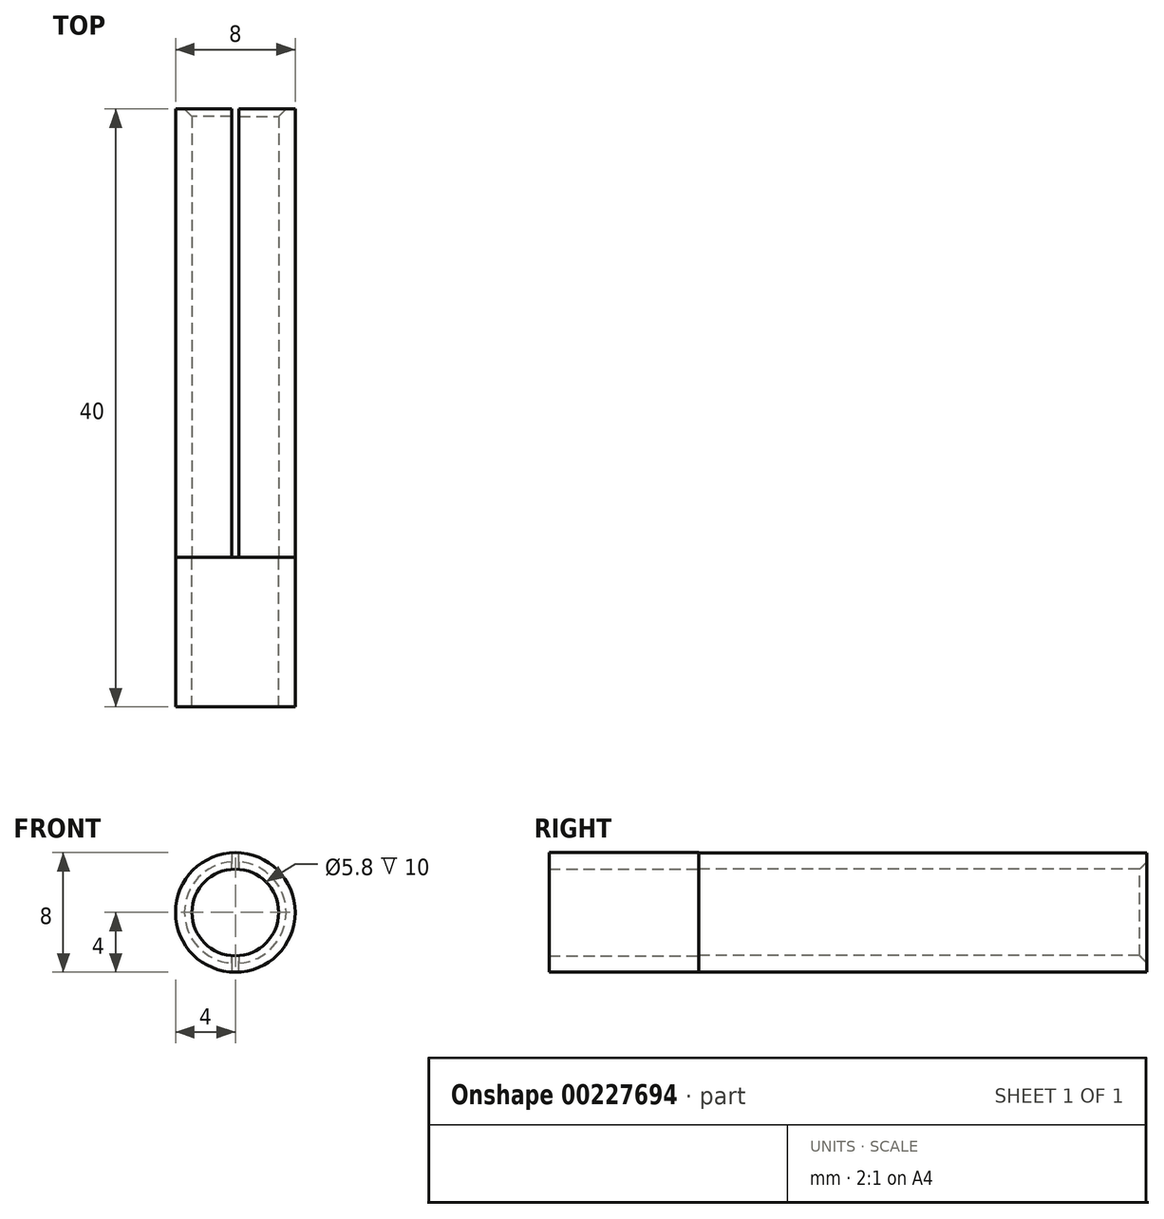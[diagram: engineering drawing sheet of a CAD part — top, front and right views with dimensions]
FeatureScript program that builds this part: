
annotation { "Feature Type Name" : "Feature", "Feature Type Description" : "" }
export const myFeature = defineFeature(function(context is Context, id is Id, definition is map)
    precondition{}
    {
        {
            var Q0;
            Q0=qCreatedBy(makeId("Front.planeOp"),FACE);
            var sketch = newSketch(context, id + "F0", { "sketchPlane" : qUnion([Q0])});
            skCircle(sketch, "E0", {"center": v(0, 0) * mm, "radius": 4 * mm});
            skCircle(sketch, "E1", {"center": v(0, 0) * mm, "radius": 2.9 * mm});
            skLineSegment(sketch, "E2", {"start": v(-0.25, 4) * mm, "end": v(-0.25, 2.89) * mm});
            skLineSegment(sketch, "E3", {"start": v(0.25, -4) * mm, "end": v(0.25, -2.89) * mm});
            skLineSegment(sketch, "E4.trimOffspring", {"start": v(-0.25, -2.89) * mm, "end": v(-0.25, -4) * mm});
            skLineSegment(sketch, "E5.trimOffspring", {"start": v(0.25, 2.89) * mm, "end": v(0.25, 4) * mm});
            skSolve(sketch);
        }
        {
            var Q0;
            {var subQ0=sQuery(id+"F0.wireOp",EDGE,"E2");Q0=makeQuery(id+"F0.imprint","IMPRINT",FACE,{"disambiguationData":[TD([[makeQuery(id+"F0.imprint","IMPRINT",EDGE,{"derivedFrom":subQ0}),-1.0]])]});}
            var Q1;
            {var subQ0=sQuery(id+"F0.wireOp",EDGE,"E3");Q1=makeQuery(id+"F0.imprint","IMPRINT",FACE,{"disambiguationData":[TD([[makeQuery(id+"F0.imprint","IMPRINT",EDGE,{"derivedFrom":subQ0}),-1.0]])]});}
            extrude(context, id + "F1", {"entities" : qUnion([Q0, Q1]), "oppositeDirection" : true, "depth" : 30 * mm});
        }
        {
            var Q0;
            {var subQ0=sQuery(id+"F0.wireOp",EDGE,"E3");Q0=makeQuery(id+"F0.imprint","IMPRINT",FACE,{"disambiguationData":[TD([[makeQuery(id+"F0.imprint","IMPRINT",EDGE,{"derivedFrom":subQ0}),-1.0]])]});}
            var Q1;
            {var subQ0=sQuery(id+"F0.wireOp",EDGE,"E2");Q1=makeQuery(id+"F0.imprint","IMPRINT",FACE,{"disambiguationData":[TD([[makeQuery(id+"F0.imprint","IMPRINT",EDGE,{"derivedFrom":subQ0}),1.0]])]});}
            var Q2;
            {var subQ0=sQuery(id+"F0.wireOp",EDGE,"E3");Q2=makeQuery(id+"F0.imprint","IMPRINT",FACE,{"disambiguationData":[TD([[makeQuery(id+"F0.imprint","IMPRINT",EDGE,{"derivedFrom":subQ0}),1.0]])]});}
            var Q3;
            {var subQ0=sQuery(id+"F0.wireOp",EDGE,"E2");Q3=makeQuery(id+"F0.imprint","IMPRINT",FACE,{"disambiguationData":[TD([[makeQuery(id+"F0.imprint","IMPRINT",EDGE,{"derivedFrom":subQ0}),-1.0]])]});}
            extrude(context, id + "F2", {"entities" : qUnion([Q0, Q1, Q2, Q3]), "depth" : 10 * mm});
        }
        {
            var Q0;
            {var subQ0=sQuery(id+"F0.wireOp",EDGE,"E1");Q0=makeQuery(id+"F1.opExtrude","CAP_EDGE",EDGE,{"disambiguationData":[OSD([subQ0]),TDD([makeQuery(id+"F0.imprint","IMPRINT",EDGE,{"disambiguationData":[TD([[makeQuery(id+"F0.imprint","INTERSECT",VERTEX,{"derivedFrom":[subQ0,sQuery(id+"F0.wireOp",EDGE,"E2")]}),-1.0]])],"derivedFrom":subQ0})])],"isStart":false});}
            var Q1;
            {var subQ0=sQuery(id+"F0.wireOp",EDGE,"E1");Q1=makeQuery(id+"F1.opExtrude","CAP_EDGE",EDGE,{"disambiguationData":[OSD([subQ0]),TDD([makeQuery(id+"F0.imprint","IMPRINT",EDGE,{"disambiguationData":[TD([[makeQuery(id+"F0.imprint","INTERSECT",VERTEX,{"derivedFrom":[subQ0,sQuery(id+"F0.wireOp",EDGE,"E3")]}),-1.0]])],"derivedFrom":subQ0})])],"isStart":false});}
            chamfer(context, id + "F3", {"entities" : qUnion([Q0, Q1]), "width" : 0.5 * mm, "tangentPropagation" : true});
        }
    });
